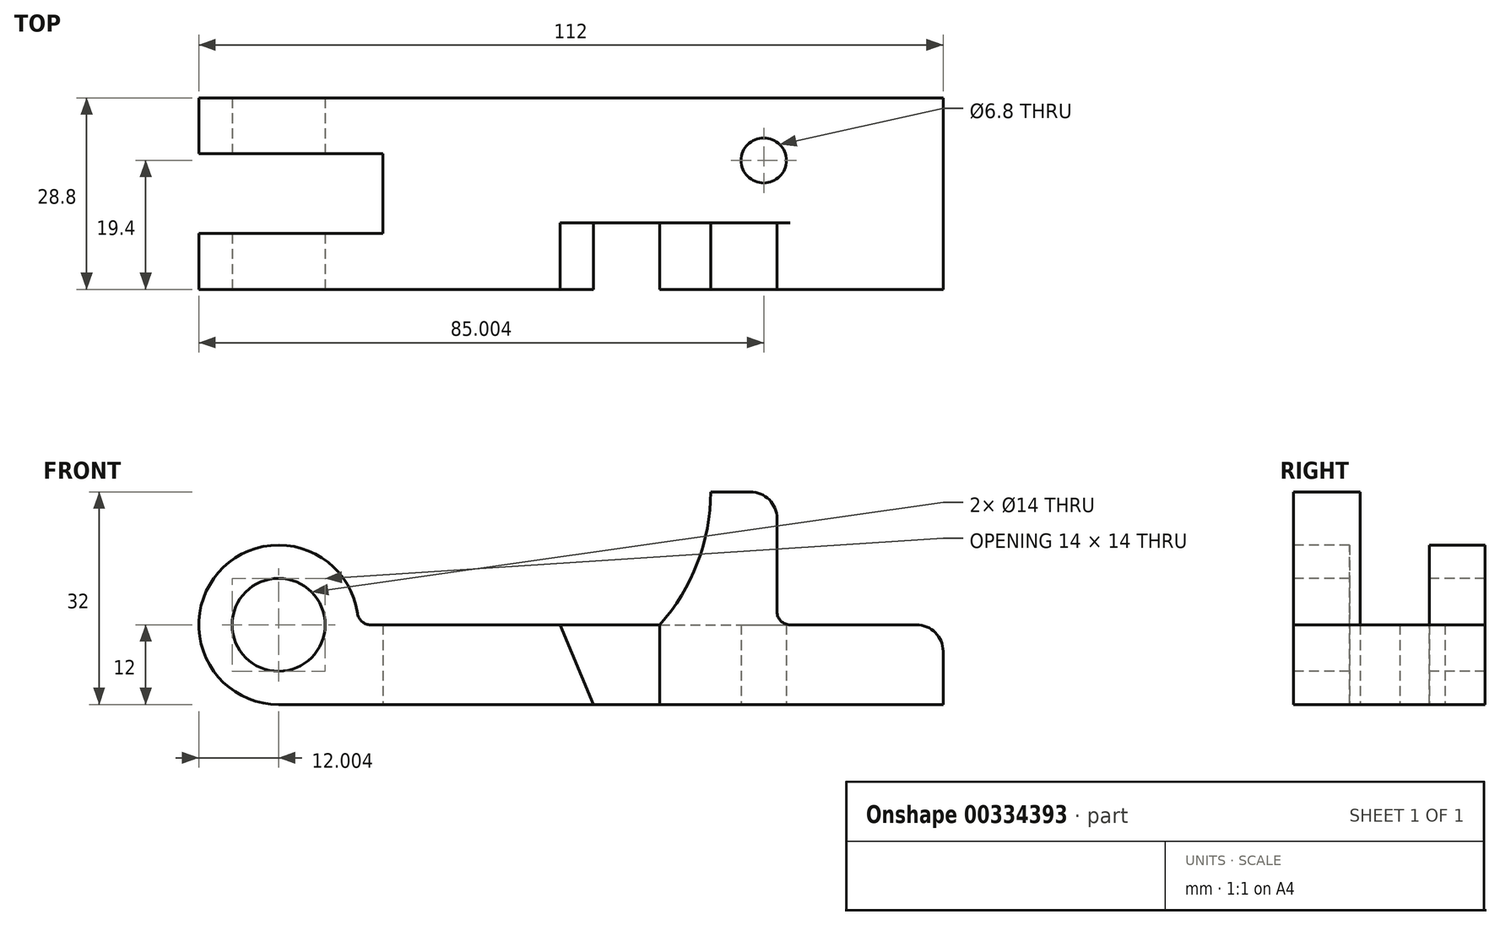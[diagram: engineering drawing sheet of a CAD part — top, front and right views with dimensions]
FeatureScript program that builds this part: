
annotation { "Feature Type Name" : "Feature", "Feature Type Description" : "" }
export const myFeature = defineFeature(function(context is Context, id is Id, definition is map)
    precondition{}
    {
        {
            var Q0;
            Q0=qCreatedBy(makeId("Front.planeOp"),FACE);
            var sketch = newSketch(context, id + "F0", { "sketchPlane" : qUnion([Q0])});
            skLineSegment(sketch, "E0", {"start": v(-52.57, 0) * mm, "end": v(47.43, 0) * mm});
            skLineSegment(sketch, "E1", {"start": v(47.43, 0) * mm, "end": v(47.43, 8) * mm});
            skLineSegment(sketch, "E2", {"start": v(43.43, 12) * mm, "end": v(24.43, 12) * mm});
            skLineSegment(sketch, "E3", {"start": v(22.43, 14) * mm, "end": v(22.43, 28) * mm});
            skLineSegment(sketch, "E4", {"start": v(18.43, 32) * mm, "end": v(12.43, 32) * mm});
            skArc(sketch, "E5", {"start": v(-40.69, 13.71) * mm, "mid": v(-61.64, 19.86) * mm, "end": v(-52.57, 0) * mm});
            skCircle(sketch, "E6", {"center": v(-52.57, 12) * mm, "radius": 7 * mm});
            skLineSegment(sketch, "E7", {"start": v(-38.7, 12) * mm, "end": v(4.8, 12) * mm});
            skPoint(sketch, "E8.visualSharp", {"position": v(47.43, 12) * mm});
            skArc(sketch, "E8.filletArc", {"start": v(47.43, 8) * mm, "mid": v(46.26, 10.83) * mm, "end": v(43.43, 12) * mm});
            skPoint(sketch, "E9.visualSharp", {"position": v(22.43, 12) * mm});
            skArc(sketch, "E9.filletArc", {"start": v(22.43, 14) * mm, "mid": v(23.02, 12.59) * mm, "end": v(24.43, 12) * mm});
            skLineSegment(sketch, "E10", {"start": v(4.8, 12) * mm, "end": v(4.8, 0) * mm});
            skLineSegment(sketch, "E11", {"start": v(-10.2, 12) * mm, "end": v(-5.2, 0) * mm});
            skPoint(sketch, "E12.visualSharp", {"position": v(-40.57, 12) * mm});
            skArc(sketch, "E12.filletArc", {"start": v(-40.69, 13.71) * mm, "mid": v(-40.02, 12.49) * mm, "end": v(-38.7, 12) * mm});
            skArc(sketch, "E13", {"start": v(4.8, 12) * mm, "mid": v(10.46, 21.3) * mm, "end": v(12.43, 32) * mm});
            skPoint(sketch, "E14.visualSharp", {"position": v(22.43, 32) * mm});
            skArc(sketch, "E14.filletArc", {"start": v(22.43, 28) * mm, "mid": v(21.26, 30.83) * mm, "end": v(18.43, 32) * mm});
            skLineSegment(sketch, "E15", {"start": v(4.8, 12) * mm, "end": v(24.43, 12) * mm});
            skSolve(sketch);
        }
        {
            var Q0;
            {var subQ3=sQuery(id+"F0.wireOp",EDGE,"E5");Q0=makeQuery(id+"F0.imprint","IMPRINT",FACE,{"disambiguationData":[TD([[makeQuery(id+"F0.imprint","IMPRINT",EDGE,{"derivedFrom":subQ3}),1.0]])]});}
            var Q1;
            {var subQ0=sQuery(id+"F0.wireOp",EDGE,"E1");Q1=makeQuery(id+"F0.imprint","IMPRINT",FACE,{"disambiguationData":[TD([[makeQuery(id+"F0.imprint","IMPRINT",EDGE,{"derivedFrom":subQ0}),1.0]])]});}
            var Q2;
            {var subQ0=sQuery(id+"F0.wireOp",EDGE,"E10");Q2=makeQuery(id+"F0.imprint","IMPRINT",FACE,{"disambiguationData":[TD([[makeQuery(id+"F0.imprint","IMPRINT",EDGE,{"derivedFrom":subQ0}),-1.0]])]});}
            extrude(context, id + "F1", {"entities" : qUnion([Q0, Q1, Q2]), "depth" : -28.8 * mm});
        }
        {
            var Q0;
            Q0=makeQuery(id+"F0.imprint","IMPRINT",FACE,{"disambiguationData":[TD([[makeQuery(id+"F0.imprint","IMPRINT",EDGE,{"derivedFrom":sQuery(id+"F0.wireOp",EDGE,"E3")}),1.0]])]});
            extrude(context, id + "F2", {"entities" : qUnion([Q0]), "operationType" : NewBodyOperationType.ADD, "depth" : -10 * mm});
        }
        {
            var Q0;
            {var subQ0=sQuery(id+"F0.wireOp",EDGE,"E10");Q0=makeQuery(id+"F0.imprint","IMPRINT",FACE,{"disambiguationData":[TD([[makeQuery(id+"F0.imprint","IMPRINT",EDGE,{"derivedFrom":subQ0}),-1.0]])]});}
            extrude(context, id + "F3", {"entities" : qUnion([Q0]), "operationType" : NewBodyOperationType.REMOVE, "oppositeDirection" : true, "depth" : 10 * mm});
        }
        {
            var Q0;
            Q0=qCreatedBy(makeId("Top.planeOp"),FACE);
            var sketch = newSketch(context, id + "F4", { "sketchPlane" : qUnion([Q0])});
            skLineSegment(sketch, "E16", {"start": v(-64.57, 0) * mm, "end": v(-64.57, 28.8) * mm});
            skLineSegment(sketch, "E17", {"start": v(-64.57, -1) * mm, "end": v(-64.57, 27.8) * mm});
            skLineSegment(sketch, "E18.0", {"start": v(-38.7, 28.8) * mm, "end": v(43.43, 28.8) * mm});
            skLineSegment(sketch, "E19.0.0", {"start": v(-10.2, 0) * mm, "end": v(-10.2, 10) * mm});
            skLineSegment(sketch, "E19.0.1", {"start": v(-10.2, 10) * mm, "end": v(4.8, 10) * mm});
            skLineSegment(sketch, "E19.0.2", {"start": v(4.8, 10) * mm, "end": v(24.43, 10) * mm});
            skLineSegment(sketch, "E19.0.3", {"start": v(24.43, 10) * mm, "end": v(24.43, 0) * mm});
            skLineSegment(sketch, "E19.0.4", {"start": v(24.43, 0) * mm, "end": v(43.43, 0) * mm});
            skLineSegment(sketch, "E19.0.5", {"start": v(43.43, 0) * mm, "end": v(43.43, 28.8) * mm});
            skLineSegment(sketch, "E19.0.6", {"start": v(43.43, 28.8) * mm, "end": v(-38.7, 28.8) * mm});
            skLineSegment(sketch, "E19.0.8", {"start": v(-38.7, 0) * mm, "end": v(-10.2, 0) * mm});
            skLineSegment(sketch, "E20", {"start": v(-64.57, 0) * mm, "end": v(-38.7, 0) * mm});
            skLineSegment(sketch, "E21", {"start": v(-64.57, 28.8) * mm, "end": v(-38.7, 28.8) * mm});
            skLineSegment(sketch, "E22", {"start": v(-64.57, 20.4) * mm, "end": v(-36.86, 20.4) * mm});
            skLineSegment(sketch, "E23", {"start": v(-64.57, 8.4) * mm, "end": v(-36.86, 8.4) * mm});
            skCircle(sketch, "E24", {"center": v(20.43, 19.4) * mm, "radius": 3.4 * mm});
            skLineSegment(sketch, "E25", {"start": v(-36.86, 20.4) * mm, "end": v(-36.86, 8.4) * mm});
            skSolve(sketch);
        }
        {
            var Q0;
            {var subQ0=sQuery(id+"F4.wireOp",EDGE,"E22");Q0=makeQuery(id+"F4.imprint","IMPRINT",FACE,{"disambiguationData":[TD([[makeQuery(id+"F4.imprint","IMPRINT",EDGE,{"derivedFrom":subQ0}),-1.0]])]});}
            var Q1;
            Q1=makeQuery(id+"F4.imprint","IMPRINT",FACE,{"disambiguationData":[TD([[makeQuery(id+"F4.imprint","IMPRINT",EDGE,{"derivedFrom":sQuery(id+"F4.wireOp",EDGE,"E24")}),1.0]])]});
            extrude(context, id + "F5", {"entities" : qUnion([Q0, Q1]), "operationType" : NewBodyOperationType.REMOVE, "depth" : 29.9 * mm});
        }
    });
